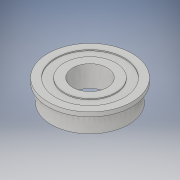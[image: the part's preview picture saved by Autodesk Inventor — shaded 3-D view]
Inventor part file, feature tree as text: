
AUTODESK INVENTOR PART (.ipt)
format: ipt  version: 2018 (Build 220112000, 112)  size: 127,488 bytes
history: native  units: in
note: dims shown in document units (in); Inventor stores cm internally (conversion verified against a paired STEP export)
features: revolve x1
ambient origin geometry x8: Origin, YZ Plane, XZ Plane, XY Plane, X Axis, Y Axis, Z Axis, Center Point
bodies: Solid1 (feature_tree)
feature tree (1):
  revolve  "Revolve1"  [1 undecoded]
note: 1 required parameter value undecoded (feature->parameter linkage not recoverable at this tier; creation-order binding heuristic only, values carry confidence <= 0.55)
